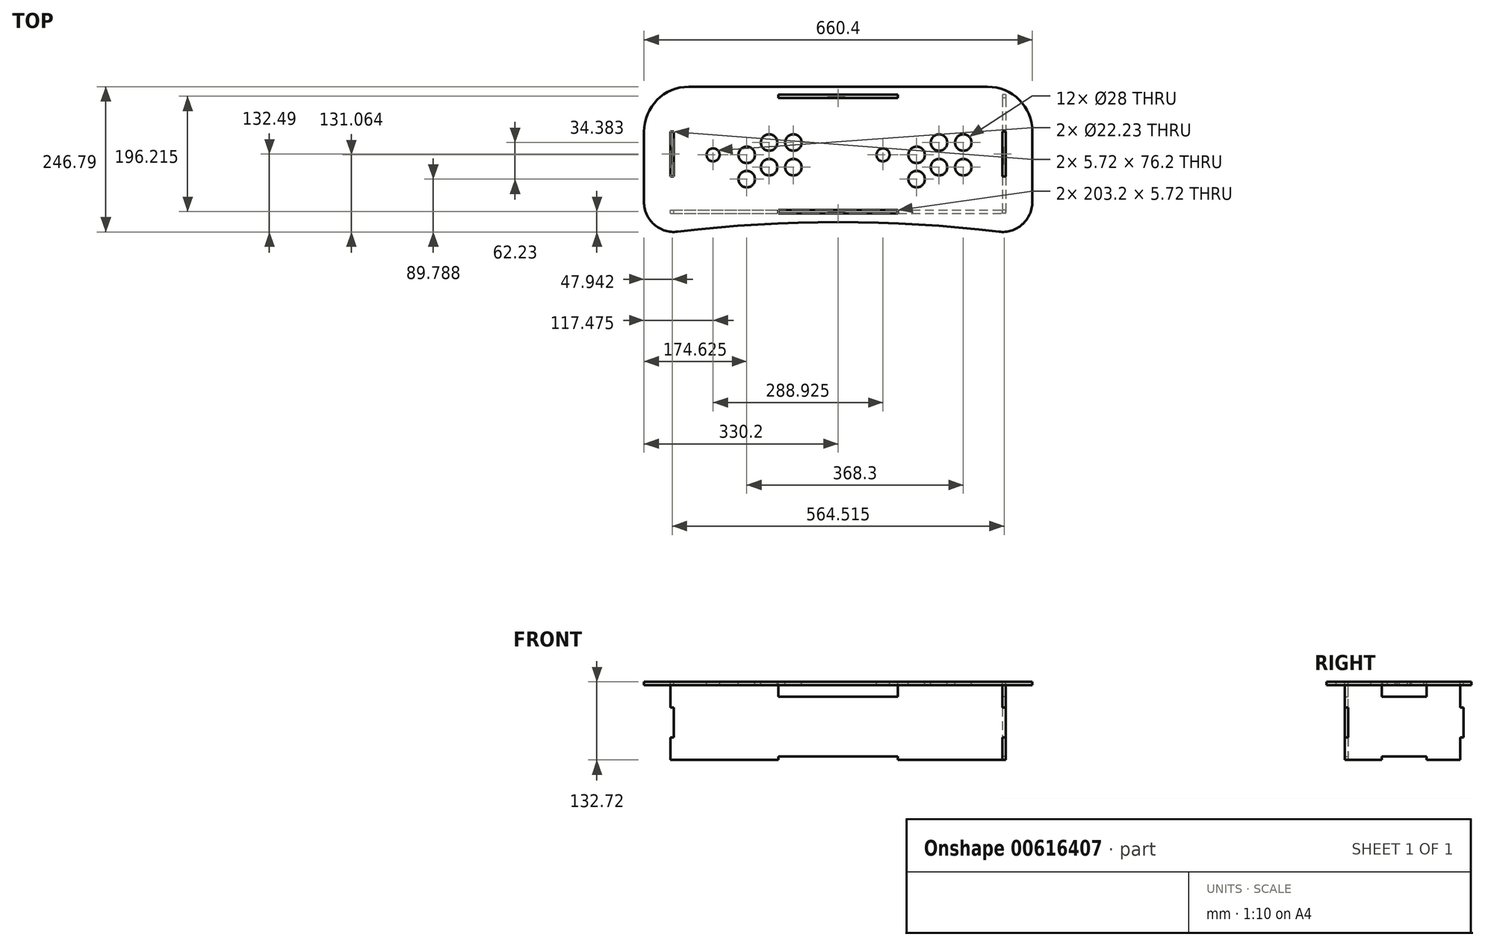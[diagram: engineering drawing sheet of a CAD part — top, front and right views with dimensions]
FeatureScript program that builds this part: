
annotation { "Feature Type Name" : "Feature", "Feature Type Description" : "" }
export const myFeature = defineFeature(function(context is Context, id is Id, definition is map)
    precondition{}
    {
        {
            var Q0;
            Q0=qCreatedBy(makeId("Top.planeOp"),FACE);
            var sketch = newSketch(context, id + "F0", { "sketchPlane" : qUnion([Q0])});
            skLineSegment(sketch, "E0.bottom", {"start": v(330.2, -127) * mm, "end": v(-330.2, -127) * mm});
            skLineSegment(sketch, "E0.top", {"start": v(330.2, 127) * mm, "end": v(-330.2, 127) * mm});
            skLineSegment(sketch, "E0.left", {"start": v(330.2, -127) * mm, "end": v(330.2, 127) * mm});
            skLineSegment(sketch, "E0.right", {"start": v(-330.2, -127) * mm, "end": v(-330.2, 127) * mm});
            skPoint(sketch, "E0.middle", {"position": v(0, 0) * mm});
            skSolve(sketch);
        }
        {
            var Q0;
            Q0=makeQuery(id+"F0.imprint","IMPRINT",FACE,{"disambiguationData":[TD([[makeQuery(id+"F0.imprint","IMPRINT",EDGE,{"derivedFrom":sQuery(id+"F0.wireOp",EDGE,"E0.bottom")}),-1.0]])]});
            extrude(context, id + "F1", {"entities" : qUnion([Q0]), "depth" : 5.7 * mm});
        }
        {
            var Q0;
            Q0=makeQuery(id+"F1.opExtrude","CAP_FACE",FACE,{"disambiguationData":[OSD([sQuery(id+"F0.wireOp",EDGE,"E0.bottom"),sQuery(id+"F0.wireOp",EDGE,"E0.top"),sQuery(id+"F0.wireOp",EDGE,"E0.left"),sQuery(id+"F0.wireOp",EDGE,"E0.right")])],"isStart":false});
            var sketch = newSketch(context, id + "F2", { "sketchPlane" : qUnion([Q0])});
            skArc(sketch, "E1", {"start": v(330.2, -127) * mm, "mid": v(0, -103.03) * mm, "end": v(-330.2, -127) * mm});
            skLineSegment(sketch, "E2", {"start": v(0, 127) * mm, "end": v(0, -127) * mm, "construction": true});
            skSolve(sketch);
        }
        {
            var Q0;
            {var subQ0=sQuery(id+"F2.wireOp",EDGE,"E1");Q0=makeQuery(id+"F2.imprint","IMPRINT",FACE,{"disambiguationData":[TD([[makeQuery(id+"F2.imprint","IMPRINT",EDGE,{"derivedFrom":subQ0}),1.0]])]});}
            extrude(context, id + "F3", {"entities" : qUnion([Q0]), "operationType" : NewBodyOperationType.REMOVE, "endBound" : BoundingType.THROUGH_ALL, "oppositeDirection" : true, "depth" : 25.4 * mm});
        }
        {
            var Q0;
            Q0=makeQuery(id+"F1.opExtrude","CAP_FACE",FACE,{"disambiguationData":[OSD([sQuery(id+"F0.wireOp",EDGE,"E0.bottom"),sQuery(id+"F0.wireOp",EDGE,"E0.top"),sQuery(id+"F0.wireOp",EDGE,"E0.left"),sQuery(id+"F0.wireOp",EDGE,"E0.right")])],"isStart":false});
            var sketch = newSketch(context, id + "F4", { "sketchPlane" : qUnion([Q0])});
            skSolve(sketch);
        }
        {
            var Q0;
            {var subQ0=sQuery(id+"F0.wireOp",EDGE,"E0.right");var subQ1=sQuery(id+"F0.wireOp",EDGE,"E0.bottom");Q0=makeQuery(id+"FBOf2KqEddd7jP7_1.boolean.opBoolean","MERGE",EDGE,{"derivedFrom":[makeQuery(id+"F1.opExtrude","SWEPT_EDGE",EDGE,{"disambiguationData":[OSD([subQ1,subQ0])]}),makeQuery(id+"FBOf2KqEddd7jP7_1.opExtrude","SWEPT_EDGE",EDGE,{"disambiguationData":[OSD([subQ1,subQ0,sQuery(id+"F4.wireOp",EDGE,"YZ262kwM-f9xy-yrOD-mAyZ-rjdBJHlWvZyA")])]})]});}
            var Q1;
            {var subQ0=sQuery(id+"F0.wireOp",EDGE,"E0.left");var subQ1=sQuery(id+"F0.wireOp",EDGE,"E0.bottom");Q1=makeQuery(id+"FBOf2KqEddd7jP7_1.boolean.opBoolean","MERGE",EDGE,{"derivedFrom":[makeQuery(id+"F1.opExtrude","SWEPT_EDGE",EDGE,{"disambiguationData":[OSD([subQ1,subQ0])]}),makeQuery(id+"FBOf2KqEddd7jP7_1.opExtrude","SWEPT_EDGE",EDGE,{"disambiguationData":[OSD([subQ1,subQ0,sQuery(id+"F4.wireOp",EDGE,"KTYkIo5P-So6Z-gEbL-5U7e-RvLePTOP2mm6")])]})]});}
            fillet(context, id + "F5", {"entities" : qUnion([Q0, Q1]), "radius" : 50.8 * mm, "tangentPropagation" : true, "allowEdgeOverflow" : false});
        }
        {
            var Q0;
            {var subQ0=sQuery(id+"F0.wireOp",EDGE,"E0.left");var subQ1=sQuery(id+"F0.wireOp",EDGE,"E0.right");Q0=makeQuery(id+"FBOf2KqEddd7jP7_1.boolean.opBoolean","MERGE",FACE,{"derivedFrom":[makeQuery(id+"F1.opExtrude","CAP_FACE",FACE,{"disambiguationData":[OSD([sQuery(id+"F0.wireOp",EDGE,"E0.bottom"),sQuery(id+"F0.wireOp",EDGE,"E0.top"),subQ0,subQ1])],"isStart":false}),makeQuery(id+"FBOf2KqEddd7jP7_1.opExtrude","CAP_FACE",FACE,{"disambiguationData":[OSD([subQ1,sQuery(id+"F4.wireOp",EDGE,"YZ262kwM-f9xy-yrOD-mAyZ-rjdBJHlWvZyA")])],"isStart":true}),makeQuery(id+"FBOf2KqEddd7jP7_1.opExtrude","CAP_FACE",FACE,{"disambiguationData":[OSD([subQ0,sQuery(id+"F4.wireOp",EDGE,"KTYkIo5P-So6Z-gEbL-5U7e-RvLePTOP2mm6")])],"isStart":true})]});}
            var sketch = newSketch(context, id + "F6", { "sketchPlane" : qUnion([Q0])});
            skLineSegment(sketch, "E3", {"start": v(0, 127) * mm, "end": v(0, -103.03) * mm, "construction": true});
            skLineSegment(sketch, "E4", {"start": v(-228.6, 11.27) * mm, "end": v(228.6, 11.27) * mm, "construction": true});
            skLineSegment(sketch, "E5", {"start": v(-212.73, 127) * mm, "end": v(-212.72, -112.95) * mm, "construction": true});
            skLineSegment(sketch, "E6", {"start": v(-117.48, 127) * mm, "end": v(-117.47, -106.05) * mm, "construction": true});
            skLineSegment(sketch, "E7", {"start": v(76.2, 127) * mm, "end": v(76.2, -104.3) * mm, "construction": true});
            skLineSegment(sketch, "E8", {"start": v(171.45, 127) * mm, "end": v(171.45, -109.46) * mm, "construction": true});
            skCircle(sketch, "E9", {"center": v(-212.72, 11.27) * mm, "radius": 11.11 * mm});
            skCircle(sketch, "E10", {"center": v(76.2, 11.27) * mm, "radius": 11.11 * mm});
            skCircle(sketch, "E11", {"center": v(-117.48, 32.23) * mm, "radius": 14 * mm});
            skCircle(sketch, "E12", {"center": v(-117.48, -9.68) * mm, "radius": 14 * mm});
            skCircle(sketch, "E13", {"center": v(-155.58, 11.27) * mm, "radius": 14 * mm});
            skCircle(sketch, "E14", {"center": v(-155.58, -30) * mm, "radius": 14 * mm});
            skCircle(sketch, "E15", {"center": v(-76.2, -9.68) * mm, "radius": 14 * mm});
            skCircle(sketch, "E16", {"center": v(-76.2, 32.23) * mm, "radius": 14 * mm});
            skCircle(sketch, "E17", {"center": v(171.45, 32.23) * mm, "radius": 14 * mm});
            skCircle(sketch, "E18", {"center": v(212.73, 32.23) * mm, "radius": 14 * mm});
            skCircle(sketch, "E19", {"center": v(212.73, -9.68) * mm, "radius": 14 * mm});
            skCircle(sketch, "E20", {"center": v(171.45, -9.68) * mm, "radius": 14 * mm});
            skCircle(sketch, "E21", {"center": v(133.35, 11.27) * mm, "radius": 14 * mm});
            skCircle(sketch, "E22", {"center": v(133.35, -30) * mm, "radius": 14 * mm});
            skLineSegment(sketch, "E23", {"start": v(-76.2, 32.23) * mm, "end": v(-76.2, -9.68) * mm, "construction": true});
            skSolve(sketch);
        }
        {
            var Q0;
            Q0=qSketchRegion(id+"F6",true);
            extrude(context, id + "F7", {"entities" : qUnion([Q0]), "operationType" : NewBodyOperationType.REMOVE, "endBound" : BoundingType.THROUGH_ALL, "oppositeDirection" : true, "depth" : 25.4 * mm});
        }
        {
            var Q0;
            Q0=makeQuery(id+"F1.opExtrude","SWEPT_EDGE",EDGE,{"disambiguationData":[OSD([sQuery(id+"F0.wireOp",EDGE,"E0.top"),sQuery(id+"F0.wireOp",EDGE,"E0.right")])]});
            var Q1;
            Q1=makeQuery(id+"F1.opExtrude","SWEPT_EDGE",EDGE,{"disambiguationData":[OSD([sQuery(id+"F0.wireOp",EDGE,"E0.top"),sQuery(id+"F0.wireOp",EDGE,"E0.left")])]});
            fillet(context, id + "F8", {"entities" : qUnion([Q0, Q1]), "radius" : 76.2 * mm, "tangentPropagation" : true, "allowEdgeOverflow" : false});
        }
        {
            var Q0;
            Q0=makeQuery(id+"F4.imprint","IMPRINT",FACE,{"disambiguationData":[TD([[makeQuery(id+"F4.imprint","IMPRINT",EDGE,{"derivedFrom":makeQuery(id+"F1.opExtrude","CAP_EDGE",EDGE,{"disambiguationData":[OSD([sQuery(id+"F0.wireOp",EDGE,"E0.top")])],"isStart":false})}),1.0]])]});
            var sketch = newSketch(context, id + "F9", { "sketchPlane" : qUnion([Q0])});
            skLineSegment(sketch, "E24.bottom", {"start": v(-279.4, -82.55) * mm, "end": v(279.4, -82.55) * mm, "construction": true});
            skLineSegment(sketch, "E24.top", {"start": v(-279.4, 107.95) * mm, "end": v(279.4, 107.95) * mm, "construction": true});
            skLineSegment(sketch, "E24.left", {"start": v(-279.4, -82.55) * mm, "end": v(-279.4, 107.95) * mm, "construction": true});
            skLineSegment(sketch, "E24.right", {"start": v(279.4, -82.55) * mm, "end": v(279.4, 107.95) * mm, "construction": true});
            skPoint(sketch, "E24.middle", {"position": v(0, 12.7) * mm});
            skSolve(sketch);
        }
        {
            var Q0;
            Q0=qCreatedBy(makeId("Front.planeOp"),FACE);
            cPlane(context, id + "F10", {"entities" : qUnion([Q0]), "cplaneType" : CPlaneType.OFFSET, "offset" : 82.55 * mm, "width" : 152.4 * mm, "height" : 152.4 * mm});
        }
        {
            var Q0;
            Q0=qCreatedBy(id+"F10.planeOp",FACE);
            var sketch = newSketch(context, id + "F11", { "sketchPlane" : qUnion([Q0])});
            skLineSegment(sketch, "E25.bottom", {"start": v(-279.4, -127) * mm, "end": v(-101.6, -127) * mm});
            skLineSegment(sketch, "E25.top", {"start": v(-279.4, 0) * mm, "end": v(-101.6, 0) * mm});
            skLineSegment(sketch, "E25.left", {"start": v(-279.4, -127) * mm, "end": v(-279.4, -88.9) * mm, "construction": true});
            skLineSegment(sketch, "E25.right", {"start": v(279.4, -127) * mm, "end": v(279.4, -88.9) * mm});
            skPoint(sketch, "E25.middle", {"position": v(0, -63.5) * mm});
            skLineSegment(sketch, "E26.bottom", {"start": v(285.12, -38.1) * mm, "end": v(279.4, -38.1) * mm});
            skLineSegment(sketch, "E26.top", {"start": v(285.12, -88.9) * mm, "end": v(279.4, -88.9) * mm});
            skLineSegment(sketch, "E26.left", {"start": v(285.11, -38.1) * mm, "end": v(285.11, -88.9) * mm});
            skPoint(sketch, "E26.middle", {"position": v(279.4, -63.5) * mm});
            skLineSegment(sketch, "E27.bottom", {"start": v(-273.69, -88.9) * mm, "end": v(-279.4, -88.9) * mm, "construction": true});
            skLineSegment(sketch, "E27.top", {"start": v(-273.69, -38.1) * mm, "end": v(-279.4, -38.1) * mm, "construction": true});
            skLineSegment(sketch, "E27.left", {"start": v(-273.69, -88.9) * mm, "end": v(-273.69, -38.1) * mm, "construction": true});
            skPoint(sketch, "E27.middle", {"position": v(-279.4, -63.5) * mm});
            skLineSegment(sketch, "E28.trimOffspring", {"start": v(-279.4, -38.1) * mm, "end": v(-279.4, 0) * mm, "construction": true});
            skLineSegment(sketch, "E29.trimOffspring", {"start": v(279.4, -38.1) * mm, "end": v(279.4, 0) * mm});
            skPoint(sketch, "E26.right.start.orphan", {"position": v(273.68, -38.1) * mm});
            skPoint(sketch, "E30.orphan", {"position": v(273.69, -88.9) * mm});
            skLineSegment(sketch, "E31.top", {"start": v(101.6, -121.28) * mm, "end": v(-101.6, -121.28) * mm});
            skLineSegment(sketch, "E31.left", {"start": v(101.6, -127) * mm, "end": v(101.6, -121.28) * mm});
            skLineSegment(sketch, "E31.right", {"start": v(-101.6, -127) * mm, "end": v(-101.6, -121.28) * mm});
            skPoint(sketch, "E31.middle", {"position": v(0, -127) * mm});
            skLineSegment(sketch, "E32.trimOffspring", {"start": v(101.6, -127) * mm, "end": v(279.4, -127) * mm});
            skPoint(sketch, "E33.orphan", {"position": v(101.6, -132.71) * mm});
            skPoint(sketch, "E34.orphan", {"position": v(-101.6, -132.71) * mm});
            skLineSegment(sketch, "E35.top", {"start": v(101.6, 5.72) * mm, "end": v(-101.6, 5.72) * mm});
            skLineSegment(sketch, "E35.left", {"start": v(101.6, 0) * mm, "end": v(101.6, 5.72) * mm});
            skLineSegment(sketch, "E35.right", {"start": v(-101.6, 0) * mm, "end": v(-101.6, 5.72) * mm});
            skPoint(sketch, "E35.middle", {"position": v(0, 0) * mm});
            skLineSegment(sketch, "E36.trimOffspring", {"start": v(101.6, 0) * mm, "end": v(279.4, 0) * mm});
            skPoint(sketch, "E37.orphan", {"position": v(101.6, -5.72) * mm});
            skPoint(sketch, "E38.orphan", {"position": v(-101.6, -5.72) * mm});
            skLineSegment(sketch, "E39", {"start": v(-285.12, 0) * mm, "end": v(-285.12, -38.1) * mm});
            skLineSegment(sketch, "E40", {"start": v(-285.12, -38.1) * mm, "end": v(-279.4, -38.1) * mm});
            skLineSegment(sketch, "E41", {"start": v(-279.4, -38.1) * mm, "end": v(-279.4, -88.9) * mm});
            skLineSegment(sketch, "E42", {"start": v(-279.4, -88.9) * mm, "end": v(-285.12, -88.9) * mm});
            skLineSegment(sketch, "E43", {"start": v(-285.12, -88.9) * mm, "end": v(-285.12, -127) * mm});
            skLineSegment(sketch, "E44", {"start": v(-285.12, 0) * mm, "end": v(-279.4, 0) * mm});
            skLineSegment(sketch, "E45", {"start": v(-285.12, -127) * mm, "end": v(-279.4, -127) * mm});
            skSolve(sketch);
        }
        {
            var Q0;
            Q0=qSketchRegion(id+"F11",true);
            extrude(context, id + "F12", {"entities" : qUnion([Q0]), "depth" : 5.7 * mm});
        }
        {
            var Q0;
            Q0=qCreatedBy(makeId("Right.planeOp"),FACE);
            cPlane(context, id + "F13", {"entities" : qUnion([Q0]), "cplaneType" : CPlaneType.OFFSET, "offset" : 279.4 * mm, "width" : 152.4 * mm, "height" : 152.4 * mm});
        }
        {
            var Q0;
            Q0=qCreatedBy(id+"F13.planeOp",FACE);
            var sketch = newSketch(context, id + "F14", { "sketchPlane" : qUnion([Q0])});
            skLineSegment(sketch, "E46", {"start": v(12.7, 5.71) * mm, "end": v(12.7, -333.33) * mm, "construction": true});
            skLineSegment(sketch, "E47.bottom", {"start": v(107.95, -127) * mm, "end": v(50.8, -127) * mm});
            skLineSegment(sketch, "E47.top", {"start": v(107.95, 0) * mm, "end": v(-82.55, 0) * mm});
            skPoint(sketch, "E47.middle", {"position": v(12.7, -63.5) * mm});
            skLineSegment(sketch, "E48", {"start": v(-82.55, -127) * mm, "end": v(-82.55, -88.9) * mm});
            skLineSegment(sketch, "E49", {"start": v(-82.55, -88.9) * mm, "end": v(-88.27, -88.9) * mm});
            skLineSegment(sketch, "E50", {"start": v(-88.27, -38.1) * mm, "end": v(-82.55, -38.1) * mm});
            skLineSegment(sketch, "E51", {"start": v(-82.55, -38.1) * mm, "end": v(-82.55, 0) * mm});
            skPoint(sketch, "E52.orphan", {"position": v(-88.27, 0) * mm});
            skLineSegment(sketch, "E53.top", {"start": v(50.8, -121.29) * mm, "end": v(-25.4, -121.29) * mm});
            skLineSegment(sketch, "E53.left", {"start": v(50.8, -127) * mm, "end": v(50.8, -121.29) * mm});
            skLineSegment(sketch, "E53.right", {"start": v(-25.4, -127) * mm, "end": v(-25.4, -121.29) * mm});
            skPoint(sketch, "E53.middle", {"position": v(12.7, -127) * mm});
            skLineSegment(sketch, "E54.trimOffspring", {"start": v(-25.4, -127) * mm, "end": v(-82.55, -127) * mm});
            skPoint(sketch, "E53.bottom.end.orphan", {"position": v(-25.4, -132.71) * mm});
            skPoint(sketch, "E55.orphan", {"position": v(50.8, -132.71) * mm});
            skLineSegment(sketch, "E56", {"start": v(-88.27, -38.1) * mm, "end": v(-88.27, 28.47) * mm});
            skLineSegment(sketch, "E57", {"start": v(-82.55, 0) * mm, "end": v(-102.92, 0) * mm});
            skLineSegment(sketch, "E58", {"start": v(-88.27, -88.9) * mm, "end": v(-88.27, -145.38) * mm});
            skLineSegment(sketch, "E59", {"start": v(-82.55, -127) * mm, "end": v(-111.14, -127) * mm});
            skLineSegment(sketch, "E60", {"start": v(-82.55, -38.1) * mm, "end": v(-82.55, -88.9) * mm});
            skLineSegment(sketch, "E61.top", {"start": v(50.8, 5.71) * mm, "end": v(-25.4, 5.71) * mm});
            skLineSegment(sketch, "E61.left", {"start": v(50.8, 0) * mm, "end": v(50.8, 5.71) * mm});
            skLineSegment(sketch, "E61.right", {"start": v(-25.4, 0) * mm, "end": v(-25.4, 5.71) * mm});
            skPoint(sketch, "E61.middle", {"position": v(12.7, 0) * mm});
            skPoint(sketch, "E62.orphan", {"position": v(-25.4, -5.72) * mm});
            skPoint(sketch, "E63.orphan", {"position": v(50.8, -5.72) * mm});
            skLineSegment(sketch, "E64", {"start": v(113.66, -38.1) * mm, "end": v(113.66, -88.9) * mm});
            skLineSegment(sketch, "E65", {"start": v(107.95, 0) * mm, "end": v(107.95, -38.1) * mm});
            skLineSegment(sketch, "E66", {"start": v(107.95, -38.1) * mm, "end": v(113.66, -38.1) * mm});
            skLineSegment(sketch, "E67", {"start": v(113.67, -88.9) * mm, "end": v(107.95, -88.9) * mm});
            skLineSegment(sketch, "E68", {"start": v(107.95, -88.9) * mm, "end": v(107.95, -127) * mm});
            skPoint(sketch, "E69.orphan", {"position": v(113.67, -127) * mm});
            skPoint(sketch, "E70.orphan", {"position": v(113.66, 0) * mm});
            skSolve(sketch);
        }
        {
            var Q0;
            Q0=qSketchRegion(id+"F14",true);
            extrude(context, id + "F15", {"entities" : qUnion([Q0]), "depth" : 5.7 * mm});
        }
        {
            var Q0;
            Q0=makeQuery(id+"F9.imprint","IMPRINT",FACE,{"disambiguationData":[TD([[makeQuery(id+"F9.imprint","IMPRINT",EDGE,{"derivedFrom":makeQuery(id+"F4.imprint","IMPRINT",EDGE,{"derivedFrom":makeQuery(id+"F1.opExtrude","CAP_EDGE",EDGE,{"disambiguationData":[OSD([sQuery(id+"F0.wireOp",EDGE,"E0.top")])],"isStart":false})})}),1.0]])]});
            var sketch = newSketch(context, id + "F16", { "sketchPlane" : qUnion([Q0])});
            skLineSegment(sketch, "E71.bottom", {"start": v(-282.26, -85.4) * mm, "end": v(282.26, -85.4) * mm, "construction": true});
            skLineSegment(sketch, "E71.top", {"start": v(-282.26, 110.8) * mm, "end": v(282.26, 110.8) * mm, "construction": true});
            skLineSegment(sketch, "E71.left", {"start": v(-282.26, -85.4) * mm, "end": v(-282.26, 110.8) * mm, "construction": true});
            skLineSegment(sketch, "E71.right", {"start": v(282.26, -85.4) * mm, "end": v(282.26, 110.8) * mm, "construction": true});
            skPoint(sketch, "E71.middle", {"position": v(0, 12.7) * mm});
            skLineSegment(sketch, "E72.bottom", {"start": v(101.6, -88.27) * mm, "end": v(-101.6, -88.26) * mm});
            skLineSegment(sketch, "E72.top", {"start": v(101.6, -82.55) * mm, "end": v(-101.6, -82.55) * mm});
            skLineSegment(sketch, "E72.left", {"start": v(101.6, -88.27) * mm, "end": v(101.6, -82.55) * mm});
            skLineSegment(sketch, "E72.right", {"start": v(-101.6, -88.27) * mm, "end": v(-101.6, -82.55) * mm});
            skPoint(sketch, "E72.middle", {"position": v(0, -85.4) * mm});
            skLineSegment(sketch, "E73.bottom", {"start": v(101.6, 107.95) * mm, "end": v(-101.6, 107.95) * mm});
            skLineSegment(sketch, "E73.top", {"start": v(101.6, 113.67) * mm, "end": v(-101.6, 113.67) * mm});
            skLineSegment(sketch, "E73.left", {"start": v(101.6, 107.95) * mm, "end": v(101.6, 113.67) * mm});
            skLineSegment(sketch, "E73.right", {"start": v(-101.6, 107.95) * mm, "end": v(-101.6, 113.67) * mm});
            skPoint(sketch, "E73.middle", {"position": v(0, 110.8) * mm});
            skLineSegment(sketch, "E74.bottom", {"start": v(285.12, -25.4) * mm, "end": v(279.4, -25.4) * mm});
            skLineSegment(sketch, "E74.top", {"start": v(285.12, 50.8) * mm, "end": v(279.4, 50.8) * mm});
            skLineSegment(sketch, "E74.left", {"start": v(285.12, -25.4) * mm, "end": v(285.12, 50.8) * mm});
            skLineSegment(sketch, "E74.right", {"start": v(279.4, -25.4) * mm, "end": v(279.4, 50.8) * mm});
            skPoint(sketch, "E74.middle", {"position": v(282.26, 12.7) * mm});
            skLineSegment(sketch, "E75.bottom", {"start": v(-279.4, -25.4) * mm, "end": v(-285.12, -25.4) * mm});
            skLineSegment(sketch, "E75.top", {"start": v(-279.4, 50.8) * mm, "end": v(-285.12, 50.8) * mm});
            skLineSegment(sketch, "E75.left", {"start": v(-279.4, -25.4) * mm, "end": v(-279.4, 50.8) * mm});
            skLineSegment(sketch, "E75.right", {"start": v(-285.12, -25.4) * mm, "end": v(-285.12, 50.8) * mm});
            skPoint(sketch, "E75.middle", {"position": v(-282.26, 12.7) * mm});
            skSolve(sketch);
        }
        {
            var Q0;
            Q0=qSketchRegion(id+"F16",true);
            extrude(context, id + "F17", {"entities" : qUnion([Q0]), "operationType" : NewBodyOperationType.REMOVE, "oppositeDirection" : true, "depth" : 25.4 * mm});
        }
        {
            var Q0;
            Q0=makeQuery(id+"F1.opExtrude","CAP_FACE",FACE,{"disambiguationData":[OSD([sQuery(id+"F0.wireOp",EDGE,"E0.bottom"),sQuery(id+"F0.wireOp",EDGE,"E0.top"),sQuery(id+"F0.wireOp",EDGE,"E0.left"),sQuery(id+"F0.wireOp",EDGE,"E0.right")])],"isStart":true});
            cPlane(context, id + "F18", {"entities" : qUnion([Q0]), "cplaneType" : CPlaneType.OFFSET, "offset" : 127 * mm, "width" : 152.4 * mm, "height" : 152.4 * mm});
        }
    });
